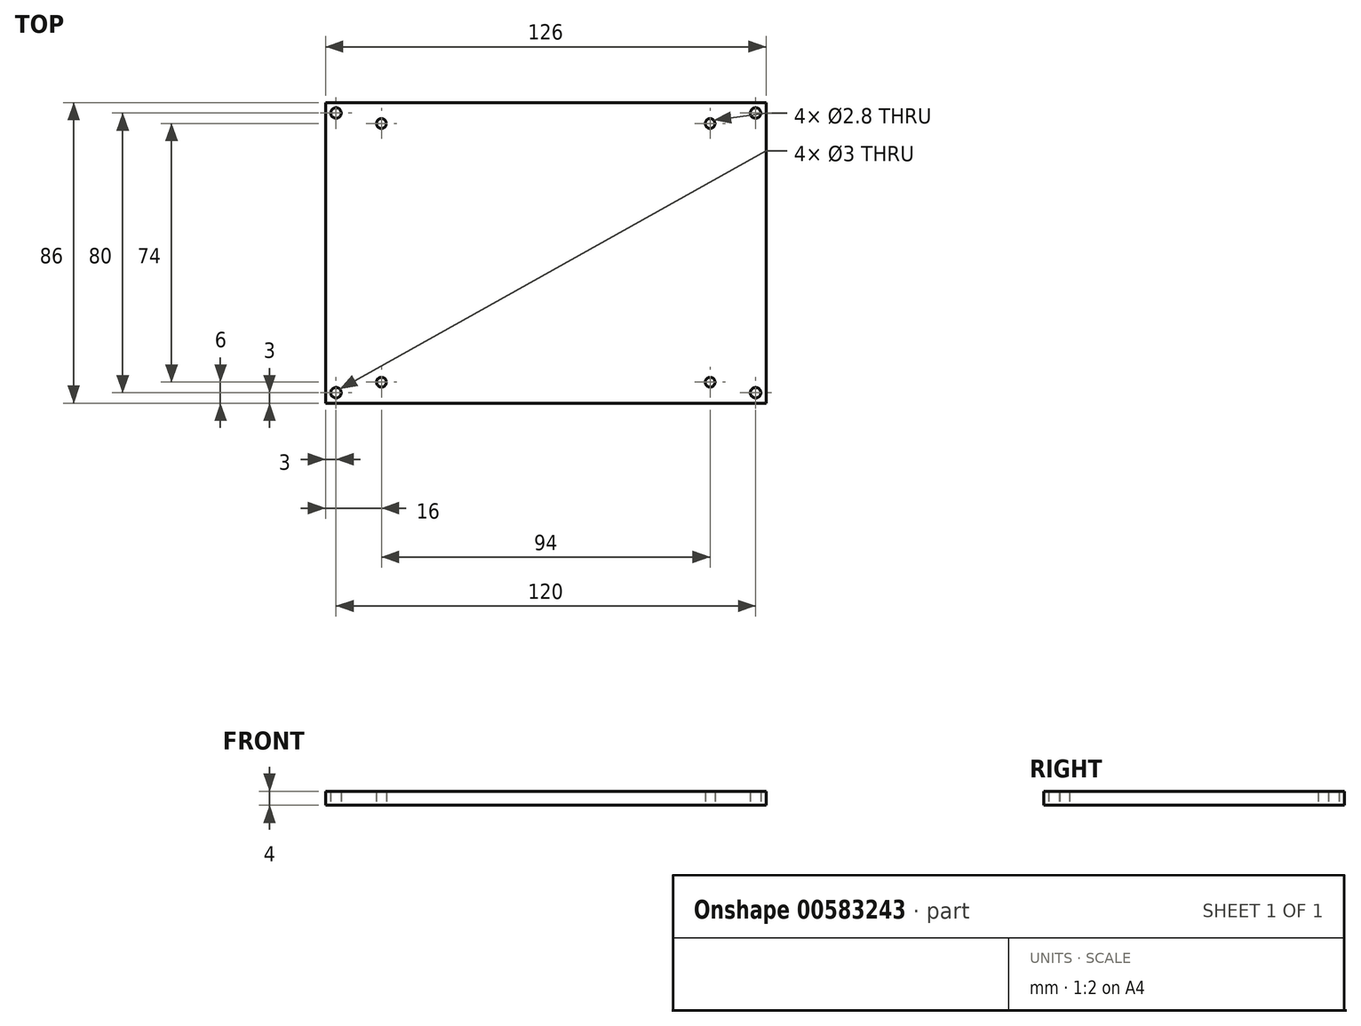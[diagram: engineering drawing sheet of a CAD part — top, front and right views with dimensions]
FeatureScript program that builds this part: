
annotation { "Feature Type Name" : "Feature", "Feature Type Description" : "" }
export const myFeature = defineFeature(function(context is Context, id is Id, definition is map)
    precondition{}
    {
        {
            var Q0;
            Q0=qCreatedBy(makeId("Top.planeOp"),FACE);
            var sketch = newSketch(context, id + "F0", { "sketchPlane" : qUnion([Q0])});
            skLineSegment(sketch, "E0.bottom", {"start": v(50, -40) * mm, "end": v(-50, -40) * mm, "construction": true});
            skLineSegment(sketch, "E0.top", {"start": v(50, 40) * mm, "end": v(-50, 40) * mm, "construction": true});
            skLineSegment(sketch, "E0.left", {"start": v(50, -40) * mm, "end": v(50, 40) * mm, "construction": true});
            skLineSegment(sketch, "E0.right", {"start": v(-50, -40) * mm, "end": v(-50, 40) * mm, "construction": true});
            skPoint(sketch, "E0.middle", {"position": v(0, 0) * mm});
            skCircle(sketch, "E1", {"center": v(-47, 37) * mm, "radius": 1.4 * mm});
            skCircle(sketch, "E2", {"center": v(47, 37) * mm, "radius": 1.4 * mm});
            skCircle(sketch, "E3", {"center": v(47, -37) * mm, "radius": 1.4 * mm});
            skCircle(sketch, "E4", {"center": v(-47, -37) * mm, "radius": 1.4 * mm});
            skLineSegment(sketch, "E5.bottom", {"start": v(63, -43) * mm, "end": v(-63, -43) * mm});
            skLineSegment(sketch, "E5.top", {"start": v(63, 43) * mm, "end": v(-63, 43) * mm});
            skLineSegment(sketch, "E5.left", {"start": v(63, -43) * mm, "end": v(63, 43) * mm});
            skLineSegment(sketch, "E5.right", {"start": v(-63, -43) * mm, "end": v(-63, 43) * mm});
            skCircle(sketch, "E6", {"center": v(-60, 40) * mm, "radius": 1.5 * mm});
            skCircle(sketch, "E7", {"center": v(-60, -40) * mm, "radius": 1.5 * mm});
            skCircle(sketch, "E8", {"center": v(60, 40) * mm, "radius": 1.5 * mm});
            skCircle(sketch, "E9", {"center": v(60, -40) * mm, "radius": 1.5 * mm});
            skSolve(sketch);
        }
        {
            var Q0;
            Q0=makeQuery(id+"F0.imprint","IMPRINT",FACE,{"disambiguationData":[TD([[makeQuery(id+"F0.imprint","IMPRINT",EDGE,{"derivedFrom":sQuery(id+"F0.wireOp",EDGE,"E1")}),-1.0]])]});
            extrude(context, id + "F1", {"entities" : qUnion([Q0]), "depth" : 4 * mm, "offsetDistance" : 25 * mm});
        }
    });
